# Revit family: Kombiventil 4006_M_SMART_LF_MF
name_source: partatom
category: Rohrzubehör
units: mm (PartAtom-declared; Revit-internal decimal feet)

## family parameters
Arbeitsebenenbasiert = Nein
Beim Laden mit Abzugskörper schneiden = Nein
Bemaßung runder Anschluss = Durchmesser verwenden
Gemeinsam genutzt = Nein
Immer vertikal = Ja
OmniClass-Nummer = 23.65.55.14
OmniClass-Titel = Valves for Liquid Services
Teiletyp = Unterbricht

## types (2) — shared parameters
Anschluss = 3/4, AG flachdichtend
Anwendungsgebiet = Das Kombiventil wird in allen pumpenbetriebenen Heiz- und Kühlanlagen eingesetzt. Der Regler begrenzt automatisch
den Volumenstrom im gewählten Anlagenteil auf den einmal eingestellten Wert, indem alle Druckschwankungen
gemessen und ausgeregelt werden. Somit sind keine Messungen erforderlich und die Regelung ist bei allen
Betriebsbedingungen effektiv. Das Kombiventil regelt den Volumenstrom der ventileigenen Voreinstellung auf einen
konstanten Wert; die Membran regelt aufgrund des Druckes unmittelbar nach dem Regeleinsatz, sowie des Druckes
davor.
B01 = 50 mm
B02 = 45.4 mm
B03 = 44.372 mm
B04 = 41.901 mm
B05 = 40.933 mm
B06 = 39.471 mm
B07 = 30.908 mm
B08 = 23.556 mm  [stored 0.0772835 ft]
B09 = 7.998 mm  [stored 0.0262402 ft]
Bauschutzkappe = Kunststoff
Druckfeder = Federstahl
E01 = 23 mm  [stored 0.0754593 ft]
E02 = 20.014 mm  [stored 0.0656627 ft]
E03 = 18.385 mm  [stored 0.0603182 ft]
E04 = 19.704 mm  [stored 0.0646457 ft]
E05 = 20.519 mm  [stored 0.0673196 ft]
E06 = 17.921 mm  [stored 0.0587959 ft]
E07 = 5.15 mm
E08 = 20.825 mm  [stored 0.0683235 ft]
E09 = 20.075 mm  [stored 0.0658629 ft]
E10 = 20.427 mm  [stored 0.0670177 ft]
E11 = 10.7 mm  [stored 0.035105 ft]
E12 = 9.001 mm
E13 = 11.063 mm  [stored 0.0362959 ft]
E14 = 20.506 mm  [stored 0.0672769 ft]
E15 = 21.877 mm  [stored 0.0717749 ft]
E16 = 23.7 mm
E17 = 28.85 mm
E18 = 5.15 mm
E19 = 5 mm  [stored 0.0164042 ft]
E20 = 108.221 mm
Gehäuse = DZR Messing CC770S
H03 = 6.351 mm  [stored 0.0208366 ft]
H04 = 12 mm  [stored 0.0393701 ft]
Hersteller = HERZ Armaturen Ges.m.b.H.
Hub = 4 mm  [stored 0.0131234 ft]
Impulsleitung = Kupfer Cu-DHP (CW024A)
L01 = 41 mm
L02 = 34 mm
L03 = 28 mm
L04 = 21 mm  [stored 0.0688976 ft]
L05 = 9 mm  [stored 0.0295276 ft]
L06 = 7 mm  [stored 0.0229659 ft]
Max. Betriebsdruck = 2500000.0 Pa
Max. Betriebstemperatur ab DN40 = 110 °C
Max. Betriebstemperatur bis DN32 = 130 °C
Max. Differenzdruck am Gehäuse = 400000.0 Pa
Medium = Wasserbeschaffenheit nach ÖNORM H 5195 und VDI 2035.
Die Verwendung von Ethylen- und Propylenglykol ist im Mischungsverhältnis 25 - 50 Vol.- [%] zulässig.
Im Hanf enthaltenes Ammoniak schädigt Messingventilgehäuse. EPDM Dichtungen werden durch Mineralöle bzw.
mineralölhaltige Schmierstoffe aufgequollen und führen somit zum Ausfall der EPDM-Dichtungen. Für Frost- und
Korrosionsschutzmittel auf der Basis von Ethylen- und Propylenglykol sind die entsprechenden Angaben den
Unterlagen des Herstellers zu entnehmen.
Gemäß Art 33 der REACH-Verordnung (EG Nr. 1907/2006) sind wir verpflichtet, darauf hinzuweisen, dass der
Stoff Blei auf der SVHC-Liste geführt wird und dass alle aus Messing bestehenden Bauteile, die in unseren
Erzeugnissen verarbeitet sind, mehr als 0,1 % (w/w) Blei (CAS: 7439-92-1 / EINECS: 231-100-4) enthalten. Da Blei
als Legierungsbestandteil fest gebunden ist, sind keine Expositionen zu erwarten und daher sind keine zusätzlichen
Angaben zur sicheren Verwendung notwendig.
Membrane = EPDM
Membrangehäuse = Messing CW602N
Min. Betriebstemperatur (Frostschutz) = -20 °C
Min. Betriebstemperatur (reines Wasser) = 2 °C
O-Ringe = EPDM
PN = 16
R02 = 4.67 mm  [stored 0.0153215 ft]
R03 = 5.755 mm  [stored 0.0188812 ft]
R04 = 7.193 mm  [stored 0.0235991 ft]
R05 = 12.954 mm  [stored 0.0425 ft]
R06 = 22 mm  [stored 0.0721785 ft]
R07 = 18.816 mm  [stored 0.0617323 ft]
R08 = 13.212 mm  [stored 0.0433465 ft]
R09 = 16.292 mm  [stored 0.0534514 ft]
R10 = 6.8 mm  [stored 0.0223097 ft]
R11 = 9.62 mm  [stored 0.0315617 ft]
R12 = 6.8 mm  [stored 0.0223097 ft]
R13 = 3.496 mm
R14 = 8.07 mm
R15 = 7.225 mm  [stored 0.0237041 ft]
S08 = 30 mm
S09 = 10 mm  [stored 0.0328084 ft]
SCRNCODE = 05;04;02
SCRNSEQ = ARM;ARM_TYP="DURR";2
Stift = Edelstahl 14301
URL = www.herz-armaturen.at
V10 = 7 mm  [stored 0.0229659 ft]
V12 = 17 mm
VRL01 = 30 mm
zero-valued in all types: Vorgabe-Ansicht

## type names (no varying parameters)
- LF
- MF

note: [stored X ft] marks values corroborated as IEEE doubles in the binary element streams (Revit-internal decimal feet)
